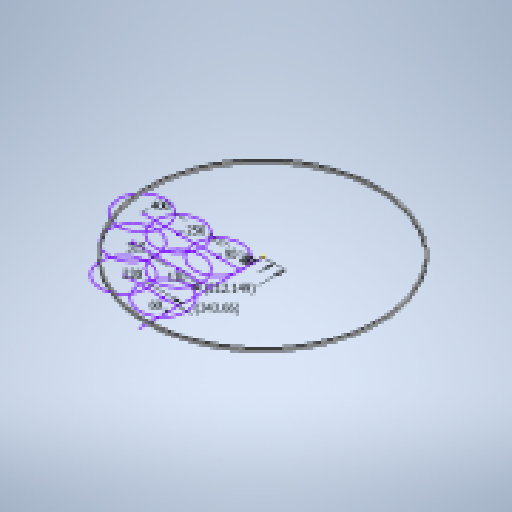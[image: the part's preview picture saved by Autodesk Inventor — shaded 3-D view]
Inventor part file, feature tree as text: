
AUTODESK INVENTOR PART (.ipt)
format: ipt  version: 2025.1 (Build 291241020, 241B)  size: 181,760 bytes
history: native  units: mm
features: sketch x3, extrude x1
ambient origin geometry x8: Origin, YZ Plane, XZ Plane, XY Plane, X Axis, Y Axis, Z Axis, Center Point
bodies: Solid1 (feature_tree)
feature tree (4):
  extrude  "Extrusion1"  Depth=6.0mm
  sketch  "Sketch2"  dims[d2=10.0mm d3=0.0mm]
  sketch  "Sketch3"  dims[d8=210.0mm d9=340.0mm d11=90.0mm d12=250.0mm d13=400.0mm d16=130.0mm d17=315.0mm d18=90.0mm d19=220.0mm d21=190.0mm d22=1200.0mm]
  sketch  "Sketch1"  dims[d0=940.0mm d1=6.0mm]
